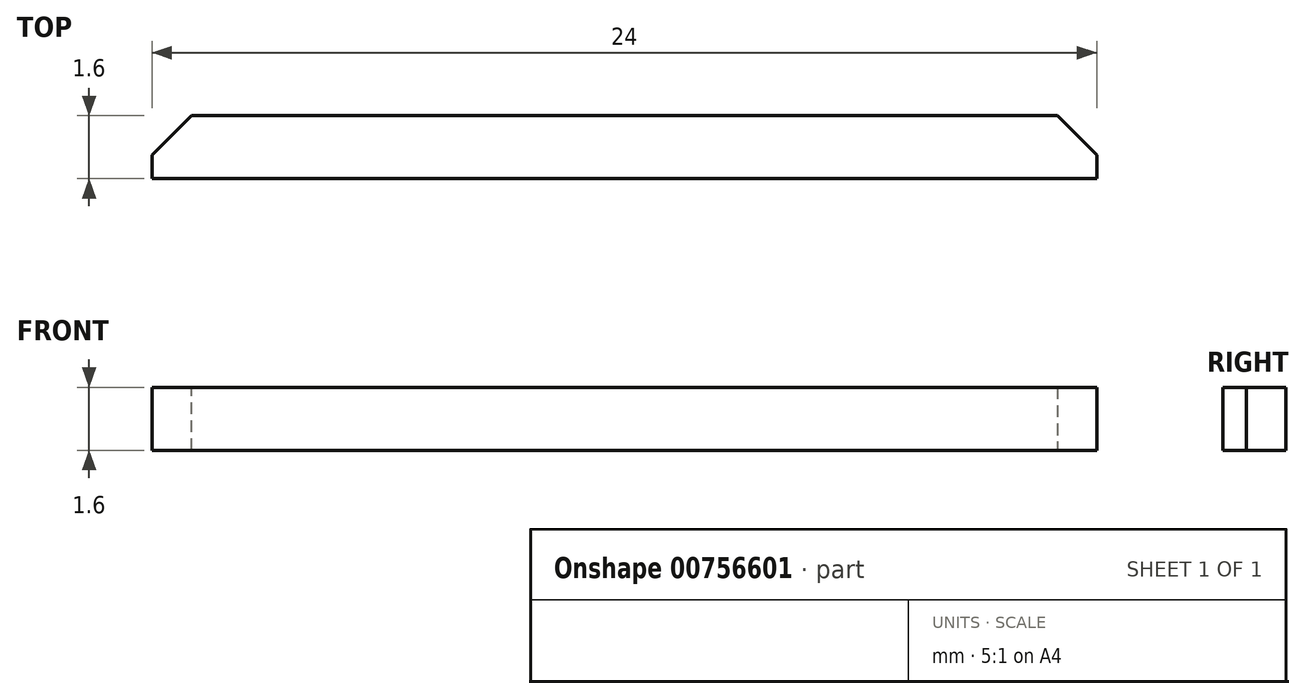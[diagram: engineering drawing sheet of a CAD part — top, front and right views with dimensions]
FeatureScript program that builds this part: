
annotation { "Feature Type Name" : "Feature", "Feature Type Description" : "" }
export const myFeature = defineFeature(function(context is Context, id is Id, definition is map)
    precondition{}
    {
        {
            var Q0;
            Q0=qCreatedBy(makeId("Top.planeOp"),FACE);
            var sketch = newSketch(context, id + "F0", { "sketchPlane" : qUnion([Q0])});
            skLineSegment(sketch, "E0.bottom", {"start": v(-29.85, 8.08) * mm, "end": v(-5.85, 8.08) * mm});
            skLineSegment(sketch, "E0.top", {"start": v(-29.85, 6.48) * mm, "end": v(-5.85, 6.48) * mm});
            skLineSegment(sketch, "E0.left", {"start": v(-29.85, 8.08) * mm, "end": v(-29.85, 6.48) * mm});
            skLineSegment(sketch, "E0.right", {"start": v(-5.85, 8.08) * mm, "end": v(-5.85, 6.48) * mm});
            skSolve(sketch);
        }
        {
            var Q0;
            Q0 = qSketchRegion(id + "F0", true);
            extrude(context, id + "F1", {"entities" : qUnion([Q0]), "depth" : 1.6 * mm, "offsetDistance" : 25 * mm});
        }
        {
            var Q0;
            Q0=makeQuery(id+"F1.opExtrude","SWEPT_EDGE",EDGE,{"disambiguationData":[OSD([sQuery(id+"F0.wireOp",EDGE,"E0.bottom"),sQuery(id+"F0.wireOp",EDGE,"E0.left")])]});
            chamfer(context, id + "F2", {"entities" : qUnion([Q0]), "chamferType" : ChamferType.TWO_OFFSETS, "width1" : 1 * mm, "oppositeDirection" : false, "width2" : 1 * mm, "tangentPropagation" : true});
        }
        {
            var Q0;
            Q0=makeQuery(id+"F1.opExtrude","SWEPT_EDGE",EDGE,{"disambiguationData":[OSD([sQuery(id+"F0.wireOp",EDGE,"E0.bottom"),sQuery(id+"F0.wireOp",EDGE,"E0.right")])]});
            chamfer(context, id + "F3", {"entities" : qUnion([Q0]), "width" : 1 * mm, "tangentPropagation" : true});
        }
    });
